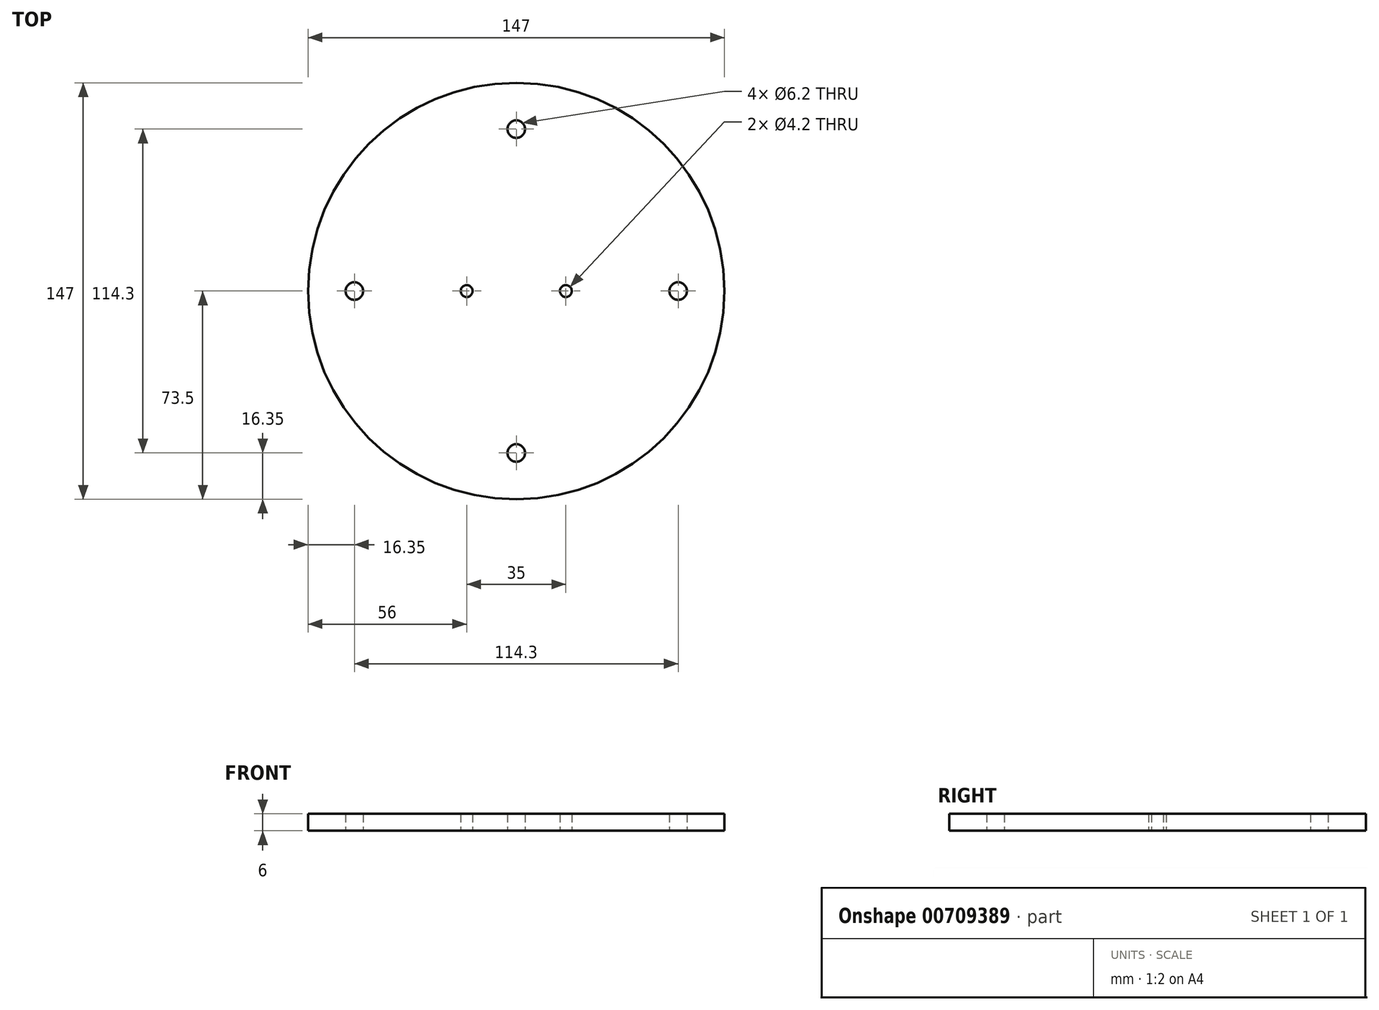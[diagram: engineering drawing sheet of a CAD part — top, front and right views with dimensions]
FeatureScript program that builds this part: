
annotation { "Feature Type Name" : "Feature", "Feature Type Description" : "" }
export const myFeature = defineFeature(function(context is Context, id is Id, definition is map)
    precondition{}
    {
        {
            var Q0;
            Q0=qCreatedBy(makeId("Top.planeOp"),FACE);
            var sketch = newSketch(context, id + "F0", { "sketchPlane" : qUnion([Q0])});
            skCircle(sketch, "E0", {"center": v(0, 0) * mm, "radius": 73.5 * mm});
            skCircle(sketch, "E1", {"center": v(57.15, 0) * mm, "radius": 3.1 * mm});
            skCircle(sketch, "E2", {"center": v(17.5, 0) * mm, "radius": 2.1 * mm});
            skCircle(sketch, "E3.1.0", {"center": v(-17.5, 0) * mm, "radius": 2.1 * mm});
            skCircle(sketch, "E4.1.0", {"center": v(0, 57.15) * mm, "radius": 3.1 * mm});
            skCircle(sketch, "E4.2.0", {"center": v(-57.15, 0) * mm, "radius": 3.1 * mm});
            skCircle(sketch, "E4.3.0", {"center": v(0, -57.15) * mm, "radius": 3.1 * mm});
            skSolve(sketch);
        }
        {
            var Q0;
            Q0=makeQuery(id+"F0.imprint","IMPRINT",FACE,{"disambiguationData":[TD([[makeQuery(id+"F0.imprint","IMPRINT",EDGE,{"derivedFrom":sQuery(id+"F0.wireOp",EDGE,"E0")}),1.0]])]});
            extrude(context, id + "F1", {"entities" : qUnion([Q0]), "depth" : 6 * mm, "offsetDistance" : 25 * mm});
        }
    });
